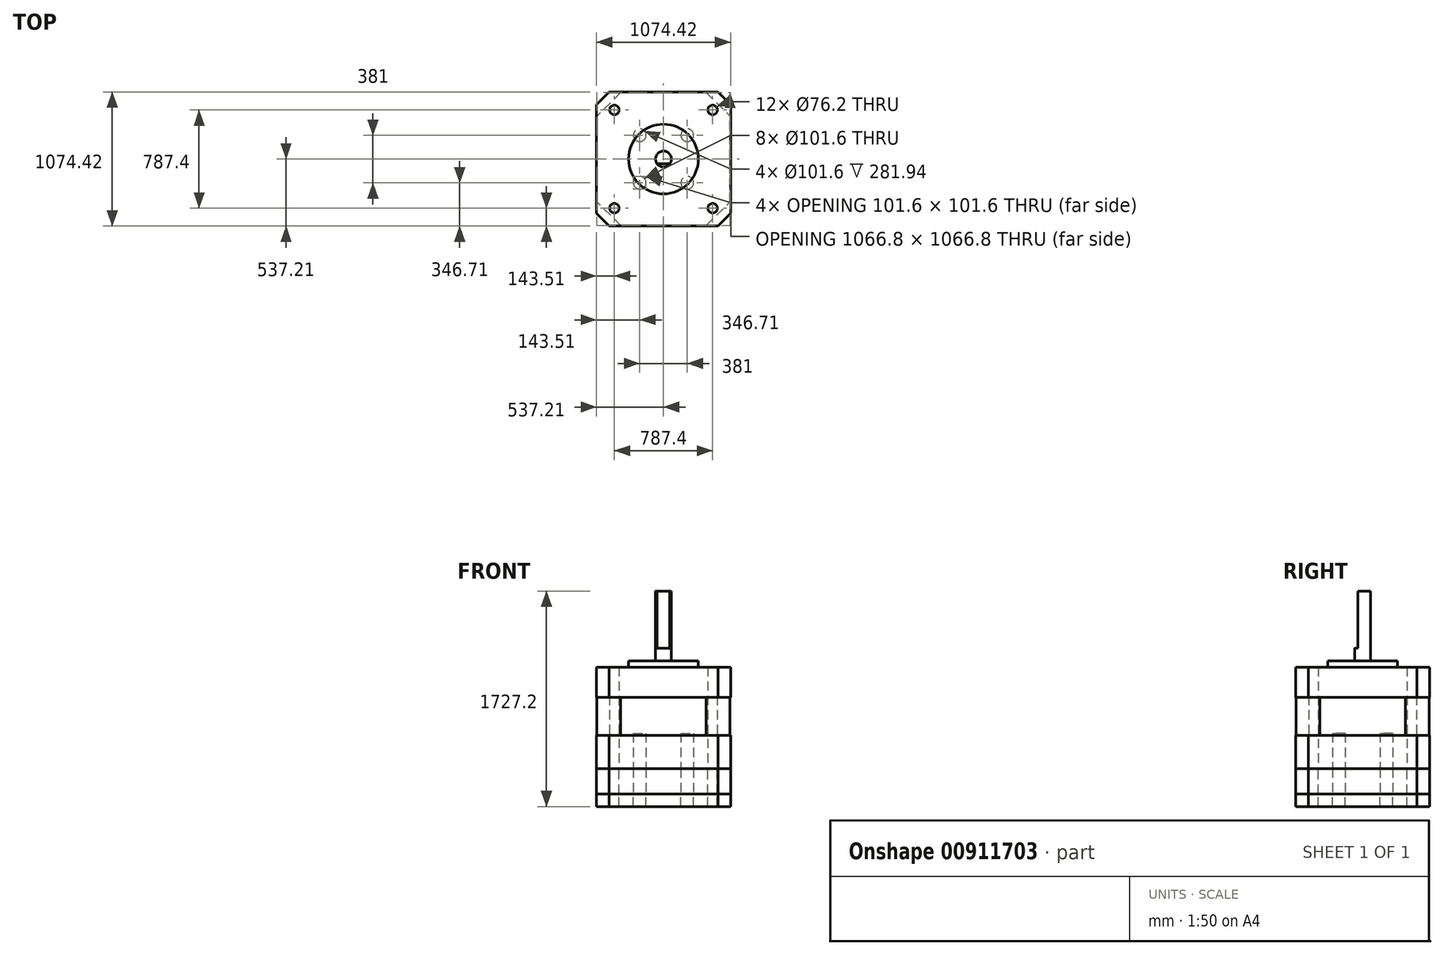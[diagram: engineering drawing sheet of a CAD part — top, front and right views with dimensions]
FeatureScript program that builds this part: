
annotation { "Feature Type Name" : "Feature", "Feature Type Description" : "" }
export const myFeature = defineFeature(function(context is Context, id is Id, definition is map)
    precondition{}
    {
        {
            var Q0;
            Q0=qCreatedBy(makeId("Top.planeOp"),FACE);
            var sketch = newSketch(context, id + "F0", { "sketchPlane" : qUnion([Q0])});
            skLineSegment(sketch, "E0.bottom", {"start": v(-537.2, -537.2) * mm, "end": v(537.2, -537.2) * mm});
            skLineSegment(sketch, "E0.top", {"start": v(-537.2, 537.2) * mm, "end": v(537.2, 537.2) * mm});
            skLineSegment(sketch, "E0.left", {"start": v(-537.2, -537.2) * mm, "end": v(-537.2, 537.2) * mm});
            skLineSegment(sketch, "E0.right", {"start": v(537.2, -537.2) * mm, "end": v(537.2, 537.2) * mm});
            skPoint(sketch, "E0.middle", {"position": v(0, 0) * mm});
            skLineSegment(sketch, "E1.bottom", {"start": v(-393.7, -393.7) * mm, "end": v(393.7, -393.7) * mm, "construction": true});
            skLineSegment(sketch, "E1.top", {"start": v(-393.7, 393.7) * mm, "end": v(393.7, 393.7) * mm, "construction": true});
            skLineSegment(sketch, "E1.left", {"start": v(-393.7, -393.7) * mm, "end": v(-393.7, 393.7) * mm, "construction": true});
            skLineSegment(sketch, "E1.right", {"start": v(393.7, -393.7) * mm, "end": v(393.7, 393.7) * mm, "construction": true});
            skCircle(sketch, "E2", {"center": v(-393.7, 393.7) * mm, "radius": 38.1 * mm});
            skCircle(sketch, "E3", {"center": v(393.7, 393.7) * mm, "radius": 38.1 * mm});
            skCircle(sketch, "E4", {"center": v(-393.7, -393.7) * mm, "radius": 38.1 * mm});
            skCircle(sketch, "E5", {"center": v(393.7, -393.7) * mm, "radius": 38.1 * mm});
            skCircle(sketch, "E6", {"center": v(0, 0) * mm, "radius": 279.4 * mm});
            skCircle(sketch, "E7", {"center": v(0, 0) * mm, "radius": 63.5 * mm});
            skLineSegment(sketch, "E8", {"start": v(0, 63.5) * mm, "end": v(0, -63.5) * mm, "construction": true});
            skLineSegment(sketch, "E9", {"start": v(-50.8, -38.1) * mm, "end": v(50.8, -38.1) * mm});
            skSolve(sketch);
        }
        {
            var Q0;
            Q0 = qSketchRegion(id + "F0", true);
            extrude(context, id + "F1", {"entities" : qUnion([Q0]), "depth" : 812.8 * mm, "offsetDistance" : 25.4 * mm});
        }
        {
            var Q0;
            Q0=makeQuery(id+"F0.imprint","IMPRINT",FACE,{"disambiguationData":[TD([[makeQuery(id+"F0.imprint","IMPRINT",EDGE,{"derivedFrom":sQuery(id+"F0.wireOp",EDGE,"E6")}),1.0]])]});
            extrude(context, id + "F2", {"entities" : qUnion([Q0]), "operationType" : NewBodyOperationType.ADD, "depth" : 1061.72 * mm - 198.12 * mm, "offsetDistance" : 25.4 * mm});
        }
        {
            var Q0;
            {var subQ0=sQuery(id+"F0.wireOp",EDGE,"E9");Q0=makeQuery(id+"F0.imprint","IMPRINT",FACE,{"disambiguationData":[TD([[makeQuery(id+"F0.imprint","IMPRINT",EDGE,{"derivedFrom":subQ0}),1.0]])]});}
            var Q1;
            {var subQ0=sQuery(id+"F0.wireOp",EDGE,"E9");Q1=makeQuery(id+"F0.imprint","IMPRINT",FACE,{"disambiguationData":[TD([[makeQuery(id+"F0.imprint","IMPRINT",EDGE,{"derivedFrom":subQ0}),-1.0]])]});}
            extrude(context, id + "F3", {"entities" : qUnion([Q0, Q1]), "operationType" : NewBodyOperationType.ADD, "depth" : 965.2 * mm, "offsetDistance" : 25.4 * mm});
        }
        {
            var Q0;
            {var subQ0=sQuery(id+"F0.wireOp",EDGE,"E9");Q0=makeQuery(id+"F0.imprint","IMPRINT",FACE,{"disambiguationData":[TD([[makeQuery(id+"F0.imprint","IMPRINT",EDGE,{"derivedFrom":subQ0}),1.0]])]});}
            extrude(context, id + "F4", {"entities" : qUnion([Q0]), "operationType" : NewBodyOperationType.ADD, "depth" : 1620.52 * mm - 198.12 * mm, "offsetDistance" : 25.4 * mm});
        }
        {
            var Q0;
            Q0=makeQuery(id+"F1.opExtrude","SWEPT_EDGE",EDGE,{"disambiguationData":[OSD([sQuery(id+"F0.wireOp",EDGE,"E0.bottom"),sQuery(id+"F0.wireOp",EDGE,"E0.left")])]});
            var Q1;
            Q1=makeQuery(id+"F1.opExtrude","SWEPT_EDGE",EDGE,{"disambiguationData":[OSD([sQuery(id+"F0.wireOp",EDGE,"E0.bottom"),sQuery(id+"F0.wireOp",EDGE,"E0.right")])]});
            var Q2;
            Q2=makeQuery(id+"F1.opExtrude","SWEPT_EDGE",EDGE,{"disambiguationData":[OSD([sQuery(id+"F0.wireOp",EDGE,"E0.top"),sQuery(id+"F0.wireOp",EDGE,"E0.right")])]});
            var Q3;
            Q3=makeQuery(id+"F1.opExtrude","SWEPT_EDGE",EDGE,{"disambiguationData":[OSD([sQuery(id+"F0.wireOp",EDGE,"E0.top"),sQuery(id+"F0.wireOp",EDGE,"E0.left")])]});
            chamfer(context, id + "F5", {"entities" : qUnion([Q0, Q1, Q2, Q3]), "width" : 101.6 * mm, "tangentPropagation" : true});
        }
        {
            var Q0;
            Q0=qCreatedBy(makeId("Top.planeOp"),FACE);
            cPlane(context, id + "F6", {"entities" : qUnion([Q0]), "cplaneType" : CPlaneType.OFFSET, "offset" : 419.1 * mm, "width" : 152.4 * mm, "height" : 152.4 * mm});
        }
        {
            var Q0;
            Q0=qCreatedBy(id+"F6.planeOp",FACE);
            var sketch = newSketch(context, id + "F7", { "sketchPlane" : qUnion([Q0])});
            skLineSegment(sketch, "E10.bottom", {"start": v(-533.4, -533.4) * mm, "end": v(533.4, -533.4) * mm});
            skLineSegment(sketch, "E10.top", {"start": v(-533.4, 533.4) * mm, "end": v(533.4, 533.4) * mm});
            skLineSegment(sketch, "E10.left", {"start": v(-533.4, -533.4) * mm, "end": v(-533.4, 533.4) * mm});
            skLineSegment(sketch, "E10.right", {"start": v(533.4, -533.4) * mm, "end": v(533.4, 533.4) * mm});
            skPoint(sketch, "E10.middle", {"position": v(0, 0) * mm});
            skLineSegment(sketch, "E11.bottom", {"start": v(-635, -635) * mm, "end": v(635, -635) * mm});
            skLineSegment(sketch, "E11.top", {"start": v(-635, 635) * mm, "end": v(635, 635) * mm});
            skLineSegment(sketch, "E11.left", {"start": v(-635, -635) * mm, "end": v(-635, 635) * mm});
            skLineSegment(sketch, "E11.right", {"start": v(635, -635) * mm, "end": v(635, 635) * mm});
            skSolve(sketch);
        }
        {
            var Q0;
            Q0 = qSketchRegion(id + "F7", true);
            extrude(context, id + "F8", {"entities" : qUnion([Q0]), "endBound" : BoundingType.SYMMETRIC, "depth" : 304.8 * mm, "offsetDistance" : 25.4 * mm});
        }
        {
            var Q0;
            Q0=makeQuery(id+"F8.opExtrude","SWEPT_EDGE",EDGE,{"disambiguationData":[OSD([sQuery(id+"F7.wireOp",EDGE,"E10.bottom"),sQuery(id+"F7.wireOp",EDGE,"E10.right")])]});
            var Q1;
            Q1=makeQuery(id+"F8.opExtrude","SWEPT_EDGE",EDGE,{"disambiguationData":[OSD([sQuery(id+"F7.wireOp",EDGE,"E10.top"),sQuery(id+"F7.wireOp",EDGE,"E10.right")])]});
            var Q2;
            Q2=makeQuery(id+"F8.opExtrude","SWEPT_EDGE",EDGE,{"disambiguationData":[OSD([sQuery(id+"F7.wireOp",EDGE,"E10.top"),sQuery(id+"F7.wireOp",EDGE,"E10.left")])]});
            var Q3;
            Q3=makeQuery(id+"F8.opExtrude","SWEPT_EDGE",EDGE,{"disambiguationData":[OSD([sQuery(id+"F7.wireOp",EDGE,"E10.bottom"),sQuery(id+"F7.wireOp",EDGE,"E10.left")])]});
            chamfer(context, id + "F9", {"entities" : qUnion([Q0, Q1, Q2, Q3]), "width" : 190.5 * mm, "tangentPropagation" : true});
        }
        {
            var Q0;
            Q0=makeQuery(id+"F8.opExtrude","SWEPT_BODY",BODY,{"disambiguationData":[OSD([sQuery(id+"F7.wireOp",EDGE,"E10.bottom"),sQuery(id+"F7.wireOp",EDGE,"E10.top"),sQuery(id+"F7.wireOp",EDGE,"E10.left"),sQuery(id+"F7.wireOp",EDGE,"E10.right"),sQuery(id+"F7.wireOp",EDGE,"E11.bottom"),sQuery(id+"F7.wireOp",EDGE,"E11.top"),sQuery(id+"F7.wireOp",EDGE,"E11.left"),sQuery(id+"F7.wireOp",EDGE,"E11.right")])]});
            var Q1;
            Q1=makeQuery(id+"F1.opExtrude","SWEPT_BODY",BODY,{"disambiguationData":[OSD([sQuery(id+"F0.wireOp",EDGE,"E0.bottom"),sQuery(id+"F0.wireOp",EDGE,"E0.top"),sQuery(id+"F0.wireOp",EDGE,"E0.left"),sQuery(id+"F0.wireOp",EDGE,"E0.right"),sQuery(id+"F0.wireOp",EDGE,"E2"),sQuery(id+"F0.wireOp",EDGE,"E3"),sQuery(id+"F0.wireOp",EDGE,"E4"),sQuery(id+"F0.wireOp",EDGE,"E5"),sQuery(id+"F0.wireOp",EDGE,"E6")])]});
            booleanBodies(context, id + "F10", {"operationType" : BooleanOperationType.SUBTRACTION, "tools" : qUnion([Q0]), "targets" : qUnion([Q1])});
        }
        {
            var Q0;
            {var subQ0=sQuery(id+"F0.wireOp",EDGE,"E7");var subQ1=sQuery(id+"F0.wireOp",EDGE,"E6");Q0=makeQuery(id+"F3.boolean.opBoolean","MERGE",FACE,{"derivedFrom":[makeQuery(id+"F2.boolean.opBoolean","MERGE",FACE,{"derivedFrom":[makeQuery(id+"F1.opExtrude","CAP_FACE",FACE,{"disambiguationData":[OSD([sQuery(id+"F0.wireOp",EDGE,"E0.bottom"),sQuery(id+"F0.wireOp",EDGE,"E0.top"),sQuery(id+"F0.wireOp",EDGE,"E0.left"),sQuery(id+"F0.wireOp",EDGE,"E0.right"),sQuery(id+"F0.wireOp",EDGE,"E2"),sQuery(id+"F0.wireOp",EDGE,"E3"),sQuery(id+"F0.wireOp",EDGE,"E4"),sQuery(id+"F0.wireOp",EDGE,"E5"),subQ1])],"isStart":true}),makeQuery(id+"F2.opExtrude","CAP_FACE",FACE,{"disambiguationData":[OSD([subQ1,subQ0])],"isStart":true})]}),makeQuery(id+"F3.opExtrude","CAP_FACE",FACE,{"disambiguationData":[OSD([subQ0])],"isStart":true})]});}
            extrude(context, id + "F11", {"entities" : qUnion([Q0]), "depth" : 203.2 * mm, "offsetDistance" : 25.4 * mm});
        }
        {
            var Q0;
            Q0=makeQuery(id+"F11.opExtrude","CAP_FACE",FACE,{"disambiguationData":[OSD([sQuery(id+"F0.wireOp",EDGE,"E0.bottom"),sQuery(id+"F0.wireOp",EDGE,"E0.top"),sQuery(id+"F0.wireOp",EDGE,"E0.left"),sQuery(id+"F0.wireOp",EDGE,"E0.right"),sQuery(id+"F0.wireOp",EDGE,"E2"),sQuery(id+"F0.wireOp",EDGE,"E3"),sQuery(id+"F0.wireOp",EDGE,"E4"),sQuery(id+"F0.wireOp",EDGE,"E5"),sQuery(id+"F0.wireOp",EDGE,"E6"),sQuery(id+"F0.wireOp",EDGE,"E7")])],"isStart":false});
            var sketch = newSketch(context, id + "F12", { "sketchPlane" : qUnion([Q0])});
            skLineSegment(sketch, "E12.bottom", {"start": v(-190.5, -190.5) * mm, "end": v(190.5, -190.5) * mm, "construction": true});
            skLineSegment(sketch, "E12.top", {"start": v(-190.5, 190.5) * mm, "end": v(190.5, 190.5) * mm, "construction": true});
            skLineSegment(sketch, "E12.left", {"start": v(-190.5, -190.5) * mm, "end": v(-190.5, 190.5) * mm, "construction": true});
            skLineSegment(sketch, "E12.right", {"start": v(190.5, -190.5) * mm, "end": v(190.5, 190.5) * mm, "construction": true});
            skPoint(sketch, "E12.middle", {"position": v(0, 0) * mm});
            skCircle(sketch, "E13", {"center": v(-190.5, 190.5) * mm, "radius": 50.8 * mm});
            skCircle(sketch, "E14", {"center": v(190.5, 190.5) * mm, "radius": 50.8 * mm});
            skCircle(sketch, "E15", {"center": v(-190.5, -190.5) * mm, "radius": 50.8 * mm});
            skCircle(sketch, "E16", {"center": v(190.5, -190.5) * mm, "radius": 50.8 * mm});
            skSolve(sketch);
        }
        {
            var Q0;
            Q0=makeQuery(id+"F12.imprint","IMPRINT",FACE,{"disambiguationData":[TD([[makeQuery(id+"F12.imprint","IMPRINT",EDGE,{"derivedFrom":sQuery(id+"F12.wireOp",EDGE,"E13")}),1.0]])]});
            var Q1;
            Q1=makeQuery(id+"F12.imprint","IMPRINT",FACE,{"disambiguationData":[TD([[makeQuery(id+"F12.imprint","IMPRINT",EDGE,{"derivedFrom":sQuery(id+"F12.wireOp",EDGE,"E14")}),1.0]])]});
            var Q2;
            Q2=makeQuery(id+"F12.imprint","IMPRINT",FACE,{"disambiguationData":[TD([[makeQuery(id+"F12.imprint","IMPRINT",EDGE,{"derivedFrom":sQuery(id+"F12.wireOp",EDGE,"E16")}),1.0]])]});
            var Q3;
            Q3=makeQuery(id+"F12.imprint","IMPRINT",FACE,{"disambiguationData":[TD([[makeQuery(id+"F12.imprint","IMPRINT",EDGE,{"derivedFrom":sQuery(id+"F12.wireOp",EDGE,"E15")}),1.0]])]});
            extrude(context, id + "F13", {"entities" : qUnion([Q0, Q1, Q2, Q3]), "operationType" : NewBodyOperationType.REMOVE, "oppositeDirection" : true, "depth" : 485.14 * mm, "offsetDistance" : 25.4 * mm});
        }
        {
            var Q0;
            Q0=makeQuery(id+"F11.opExtrude","CAP_FACE",FACE,{"disambiguationData":[OSD([sQuery(id+"F0.wireOp",EDGE,"E0.bottom"),sQuery(id+"F0.wireOp",EDGE,"E0.top"),sQuery(id+"F0.wireOp",EDGE,"E0.left"),sQuery(id+"F0.wireOp",EDGE,"E0.right"),sQuery(id+"F0.wireOp",EDGE,"E2"),sQuery(id+"F0.wireOp",EDGE,"E3"),sQuery(id+"F0.wireOp",EDGE,"E4"),sQuery(id+"F0.wireOp",EDGE,"E5"),sQuery(id+"F0.wireOp",EDGE,"E6"),sQuery(id+"F0.wireOp",EDGE,"E7")])],"isStart":false});
            extrude(context, id + "F14", {"entities" : qUnion([Q0]), "depth" : 101.6 * mm, "offsetDistance" : 25.4 * mm});
        }
    });
